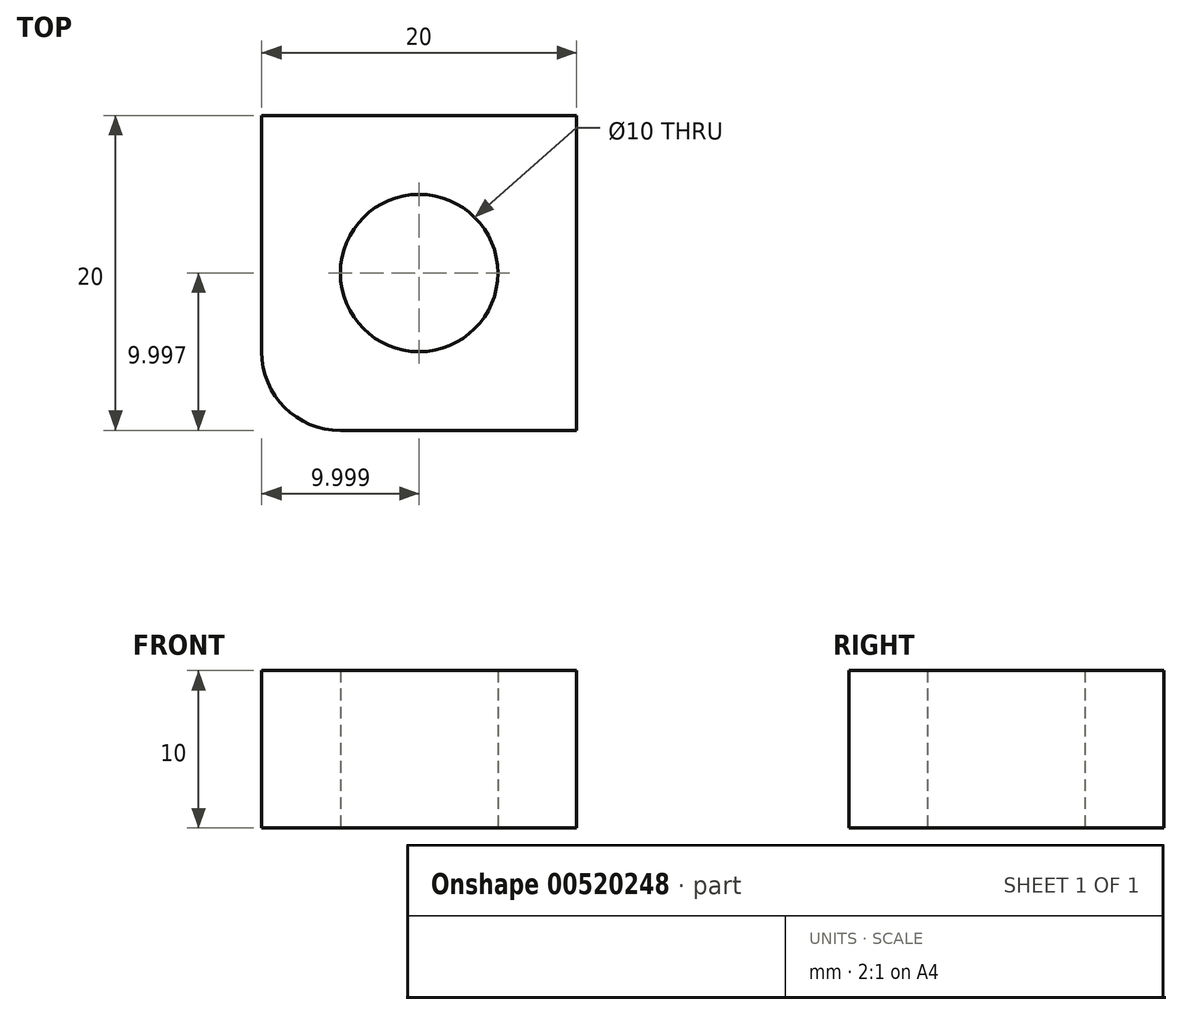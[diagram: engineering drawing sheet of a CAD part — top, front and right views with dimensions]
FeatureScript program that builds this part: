
annotation { "Feature Type Name" : "Feature", "Feature Type Description" : "" }
export const myFeature = defineFeature(function(context is Context, id is Id, definition is map)
    precondition{}
    {
        {
            var Q0;
            Q0=qCreatedBy(makeId("Top.planeOp"),FACE);
            var sketch = newSketch(context, id + "F0", { "sketchPlane" : qUnion([Q0])});
            skLineSegment(sketch, "E0.bottom", {"start": v(10.08, 10.04) * mm, "end": v(-9.92, 10.04) * mm});
            skLineSegment(sketch, "E0.top", {"start": v(10.08, -9.96) * mm, "end": v(-9.92, -9.96) * mm});
            skLineSegment(sketch, "E0.left", {"start": v(10.08, 10.04) * mm, "end": v(10.08, -9.96) * mm});
            skLineSegment(sketch, "E0.right", {"start": v(-9.92, 10.04) * mm, "end": v(-9.92, -9.96) * mm});
            skCircle(sketch, "E1", {"center": v(0.08, 0.04) * mm, "radius": 5 * mm});
            skSolve(sketch);
        }
        {
            var Q0;
            Q0=makeQuery(id+"F0.imprint","IMPRINT",FACE,{"disambiguationData":[TD([[makeQuery(id+"F0.imprint","IMPRINT",EDGE,{"derivedFrom":sQuery(id+"F0.wireOp",EDGE,"E0.bottom")}),1.0]])]});
            extrude(context, id + "F1", {"entities" : qUnion([Q0]), "depth" : 10 * mm, "offsetDistance" : 25 * mm});
        }
        {
            var Q0;
            Q0=makeQuery(id+"F1.opExtrude","SWEPT_EDGE",EDGE,{"disambiguationData":[OSD([sQuery(id+"F0.wireOp",EDGE,"E0.top"),sQuery(id+"F0.wireOp",EDGE,"E0.right")])]});
            fillet(context, id + "F2", {"entities" : qUnion([Q0]), "radius" : 5 * mm, "tangentPropagation" : true, "allowEdgeOverflow" : false});
        }
    });
